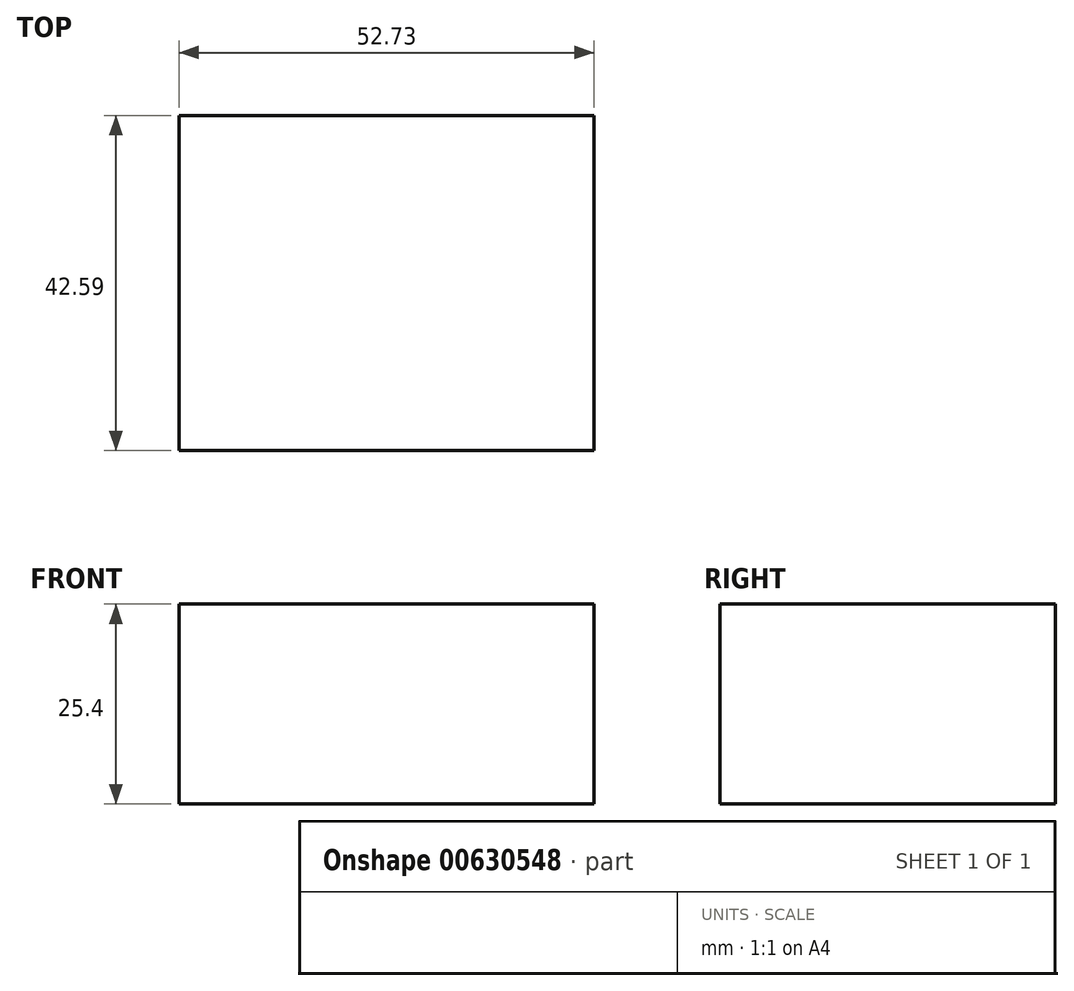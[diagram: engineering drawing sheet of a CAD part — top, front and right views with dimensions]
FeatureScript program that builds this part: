
annotation { "Feature Type Name" : "Feature", "Feature Type Description" : "" }
export const myFeature = defineFeature(function(context is Context, id is Id, definition is map)
    precondition{}
    {
        {
            var Q0;
            Q0=qCreatedBy(makeId("Top.planeOp"),FACE);
            var sketch = newSketch(context, id + "F0", { "sketchPlane" : qUnion([Q0])});
            skLineSegment(sketch, "E0.bottom", {"start": v(0, 0) * mm, "end": v(52.73, 0) * mm});
            skLineSegment(sketch, "E0.top", {"start": v(0, 42.6) * mm, "end": v(52.73, 42.6) * mm});
            skLineSegment(sketch, "E0.left", {"start": v(0, 0) * mm, "end": v(0, 42.6) * mm});
            skLineSegment(sketch, "E0.right", {"start": v(52.73, 0) * mm, "end": v(52.73, 42.6) * mm});
            skSolve(sketch);
        }
        {
            var Q0;
            Q0 = qSketchRegion(id + "F0", true);
            extrude(context, id + "F1", {"entities" : qUnion([Q0]), "depth" : 25.4 * mm, "offsetDistance" : 25.4 * mm});
        }
    });
